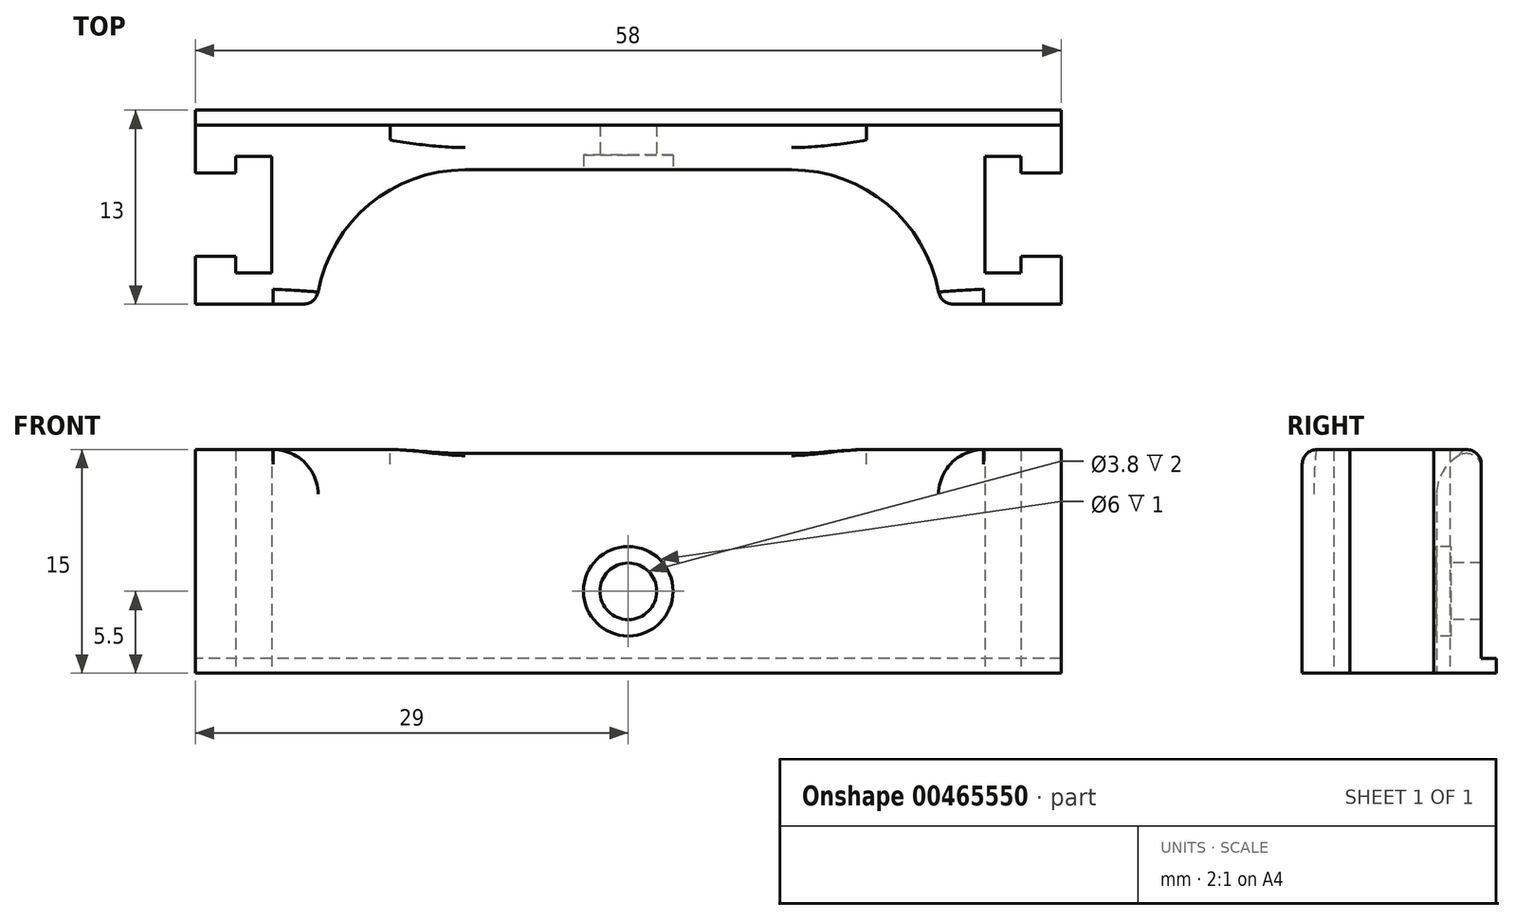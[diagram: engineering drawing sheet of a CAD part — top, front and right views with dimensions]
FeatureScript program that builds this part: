
annotation { "Feature Type Name" : "Feature", "Feature Type Description" : "" }
export const myFeature = defineFeature(function(context is Context, id is Id, definition is map)
    precondition{}
    {
        {
            var Q0;
            Q0=qCreatedBy(makeId("Front.planeOp"),FACE);
            var sketch = newSketch(context, id + "F0", { "sketchPlane" : qUnion([Q0])});
            skLineSegment(sketch, "E0.bottom", {"start": v(29, 15) * mm, "end": v(-29, 15) * mm});
            skLineSegment(sketch, "E0.top", {"start": v(29, 0) * mm, "end": v(-29, 0) * mm});
            skLineSegment(sketch, "E0.left", {"start": v(29, 15) * mm, "end": v(29, 0) * mm});
            skLineSegment(sketch, "E0.right", {"start": v(-29, 15) * mm, "end": v(-29, 0) * mm});
            skSolve(sketch);
        }
        {
            var Q0;
            Q0=qCreatedBy(makeId("Front.planeOp"),FACE);
            var sketch = newSketch(context, id + "F1", { "sketchPlane" : qUnion([Q0])});
            skLineSegment(sketch, "E1.bottom", {"start": v(29, 1) * mm, "end": v(-29, 1) * mm});
            skLineSegment(sketch, "E1.top", {"start": v(29, 0) * mm, "end": v(-29, 0) * mm});
            skLineSegment(sketch, "E1.left", {"start": v(29, 1) * mm, "end": v(29, 0) * mm});
            skLineSegment(sketch, "E1.right", {"start": v(-29, 1) * mm, "end": v(-29, 0) * mm});
            skSolve(sketch);
        }
        {
            var Q0;
            Q0 = qSketchRegion(id + "F0", true);
            extrude(context, id + "F2", {"entities" : qUnion([Q0]), "depth" : 12 * mm});
        }
        {
            var Q0;
            Q0=qCreatedBy(makeId("Top.planeOp"),FACE);
            var sketch = newSketch(context, id + "F3", { "sketchPlane" : qUnion([Q0])});
            skLineSegment(sketch, "E2", {"start": v(-29, -3.2) * mm, "end": v(-26.3, -3.2) * mm});
            skLineSegment(sketch, "E3", {"start": v(-26.3, -3.2) * mm, "end": v(-26.3, -2.1) * mm});
            skLineSegment(sketch, "E4", {"start": v(-26.3, -2.1) * mm, "end": v(-23.9, -2.1) * mm});
            skLineSegment(sketch, "E5", {"start": v(-23.9, -2.1) * mm, "end": v(-23.9, -9.9) * mm});
            skLineSegment(sketch, "E6", {"start": v(-23.9, -9.9) * mm, "end": v(-26.3, -9.9) * mm});
            skLineSegment(sketch, "E7", {"start": v(-26.3, -9.9) * mm, "end": v(-26.3, -8.8) * mm});
            skLineSegment(sketch, "E8", {"start": v(-26.3, -8.8) * mm, "end": v(-29, -8.8) * mm});
            skLineSegment(sketch, "E9", {"start": v(-29, -8.8) * mm, "end": v(-29, -3.2) * mm});
            skLineSegment(sketch, "E10", {"start": v(29, -3.2) * mm, "end": v(26.3, -3.2) * mm});
            skLineSegment(sketch, "E11", {"start": v(26.3, -3.2) * mm, "end": v(26.3, -2.1) * mm});
            skLineSegment(sketch, "E12", {"start": v(26.3, -2.1) * mm, "end": v(23.9, -2.1) * mm});
            skLineSegment(sketch, "E13", {"start": v(23.9, -2.1) * mm, "end": v(23.9, -9.9) * mm});
            skLineSegment(sketch, "E14", {"start": v(23.9, -9.9) * mm, "end": v(26.3, -9.9) * mm});
            skLineSegment(sketch, "E15", {"start": v(26.3, -9.9) * mm, "end": v(26.3, -8.8) * mm});
            skLineSegment(sketch, "E16", {"start": v(26.3, -8.8) * mm, "end": v(29, -8.8) * mm});
            skLineSegment(sketch, "E17", {"start": v(29, -8.8) * mm, "end": v(29, -3.2) * mm});
            skSolve(sketch);
        }
        {
            var Q0;
            Q0 = qSketchRegion(id + "F3", true);
            extrude(context, id + "F4", {"entities" : qUnion([Q0]), "operationType" : NewBodyOperationType.REMOVE, "depth" : 25 * mm});
        }
        {
            var Q0;
            Q0=qCreatedBy(makeId("Top.planeOp"),FACE);
            var sketch = newSketch(context, id + "F5", { "sketchPlane" : qUnion([Q0])});
            skLineSegment(sketch, "E18.bottom", {"start": v(-20.9, -3) * mm, "end": v(20.9, -3) * mm});
            skLineSegment(sketch, "E18.top", {"start": v(-20.9, -12) * mm, "end": v(20.9, -12) * mm});
            skLineSegment(sketch, "E18.left", {"start": v(-20.9, -3) * mm, "end": v(-20.9, -12) * mm});
            skLineSegment(sketch, "E18.right", {"start": v(20.9, -3) * mm, "end": v(20.9, -12) * mm});
            skSolve(sketch);
        }
        {
            var Q0;
            Q0 = qSketchRegion(id + "F5", true);
            extrude(context, id + "F6", {"entities" : qUnion([Q0]), "operationType" : NewBodyOperationType.REMOVE, "depth" : 25 * mm});
        }
        {
            var Q0;
            Q0=makeQuery(id+"F6.boolean.opBoolean","COPY",FACE,{"derivedFrom":makeQuery(id+"F6.opExtrude","SWEPT_FACE",FACE,{"disambiguationData":[OSD([sQuery(id+"F5.wireOp",EDGE,"E18.bottom")])]})});
            var sketch = newSketch(context, id + "F7", { "sketchPlane" : qUnion([Q0])});
            skPoint(sketch, "E19", {"position": v(0, 5.5) * mm});
            skSolve(sketch);
        }
        {
            var Q0;
            Q0 = qSketchRegion(id + "F1", true);
            extrude(context, id + "F8", {"entities" : qUnion([Q0]), "operationType" : NewBodyOperationType.ADD, "oppositeDirection" : true, "depth" : 1 * mm});
        }
        {
            var Q0;
            Q0=sQuery(id+"F7.wireOp",VERTEX,"E19");
            var Q1;
            Q1=makeQuery(id+"F2.opExtrude","SWEPT_BODY",BODY,{"disambiguationData":[OSD([sQuery(id+"F0.wireOp",EDGE,"E0.bottom"),sQuery(id+"F0.wireOp",EDGE,"E0.top"),sQuery(id+"F0.wireOp",EDGE,"E0.left"),sQuery(id+"F0.wireOp",EDGE,"E0.right")])]});
            hole(context, id + "F9", {"style" : HoleStyle.C_BORE, "endStyle" : HoleEndStyle.THROUGH, "holeDiameter" : 3.8 * mm, "cBoreDiameter" : 6 * mm, "cBoreDepth" : 1 * mm, "tappedDepth" : 12 * mm, "tapClearance" : 3, "locations" : qUnion([Q0]), "scope" : qUnion([Q1])});
        }
        {
            var Q0;
            Q0=makeQuery(id+"F6.boolean.opBoolean","COPY",EDGE,{"derivedFrom":makeQuery(id+"F6.opExtrude","SWEPT_EDGE",EDGE,{"disambiguationData":[OSD([sQuery(id+"F5.wireOp",EDGE,"E18.bottom"),sQuery(id+"F5.wireOp",EDGE,"E18.left")])]})});
            var Q1;
            Q1=makeQuery(id+"F6.boolean.opBoolean","COPY",EDGE,{"derivedFrom":makeQuery(id+"F6.opExtrude","SWEPT_EDGE",EDGE,{"disambiguationData":[OSD([sQuery(id+"F5.wireOp",EDGE,"E18.bottom"),sQuery(id+"F5.wireOp",EDGE,"E18.right")])]})});
            fillet(context, id + "F10", {"entities" : qUnion([Q0, Q1]), "radius" : 10 * mm, "tangentPropagation" : true, "allowEdgeOverflow" : false});
        }
        {
            var Q0;
            Q0=makeQuery(id+"F6.boolean.opBoolean","INTERSECT",EDGE,{"derivedFrom":[makeQuery(id+"F2.opExtrude","SWEPT_FACE",FACE,{"disambiguationData":[OSD([sQuery(id+"F0.wireOp",EDGE,"E0.bottom")])]}),makeQuery(id+"F6.opExtrude","SWEPT_FACE",FACE,{"disambiguationData":[OSD([sQuery(id+"F5.wireOp",EDGE,"E18.bottom")])]})]});
            fillet(context, id + "F11", {"entities" : qUnion([Q0]), "radius" : 3 * mm, "tangentPropagation" : true, "allowEdgeOverflow" : false});
        }
        {
            var Q0;
            {var subQ0=sQuery(id+"F0.wireOp",EDGE,"E0.bottom");var subQ1=sQuery(id+"F0.wireOp",EDGE,"E0.right");Q0=makeQuery(id+"F6.boolean.opBoolean","SPLIT",EDGE,{"disambiguationData":[TD([makeQuery(id+"F2.opExtrude","SWEPT_FACE",FACE,{"disambiguationData":[OSD([subQ1])]})])],"derivedFrom":makeQuery(id+"F2.opExtrude","CAP_EDGE",EDGE,{"disambiguationData":[OSD([subQ0])],"isStart":false})});}
            var Q1;
            {var subQ0=sQuery(id+"F0.wireOp",EDGE,"E0.bottom");var subQ1=sQuery(id+"F0.wireOp",EDGE,"E0.left");Q1=makeQuery(id+"F6.boolean.opBoolean","SPLIT",EDGE,{"disambiguationData":[TD([makeQuery(id+"F2.opExtrude","SWEPT_FACE",FACE,{"disambiguationData":[OSD([subQ1])]})])],"derivedFrom":makeQuery(id+"F2.opExtrude","CAP_EDGE",EDGE,{"disambiguationData":[OSD([subQ0])],"isStart":false})});}
            fillet(context, id + "F12", {"entities" : qUnion([Q0, Q1]), "radius" : 1 * mm, "tangentPropagation" : true, "allowEdgeOverflow" : false});
        }
        {
            var Q0;
            {var subQ0=sQuery(id+"F0.wireOp",EDGE,"E0.bottom");Q0=makeQuery(id+"F11.opFillet","BLEND_EDGE",EDGE,{"blendedFrom":[makeQuery(id+"F6.boolean.opBoolean","INTERSECT",EDGE,{"derivedFrom":[makeQuery(id+"F2.opExtrude","SWEPT_FACE",FACE,{"disambiguationData":[OSD([subQ0])]}),makeQuery(id+"F6.opExtrude","SWEPT_FACE",FACE,{"disambiguationData":[OSD([sQuery(id+"F5.wireOp",EDGE,"E18.bottom")])]})]}),makeQuery(id+"F2.opExtrude","CAP_FACE",FACE,{"disambiguationData":[OSD([subQ0,sQuery(id+"F0.wireOp",EDGE,"E0.top"),sQuery(id+"F0.wireOp",EDGE,"E0.left"),sQuery(id+"F0.wireOp",EDGE,"E0.right")])],"isStart":true})],"blendedInto":[makeQuery(id+"F2.opExtrude","CAP_FACE",FACE,{"disambiguationData":[OSD([subQ0,sQuery(id+"F0.wireOp",EDGE,"E0.top"),sQuery(id+"F0.wireOp",EDGE,"E0.left"),sQuery(id+"F0.wireOp",EDGE,"E0.right")])],"isStart":true})]});}
            fillet(context, id + "F13", {"entities" : qUnion([Q0]), "radius" : 1 * mm, "tangentPropagation" : true, "allowEdgeOverflow" : false});
        }
    });
